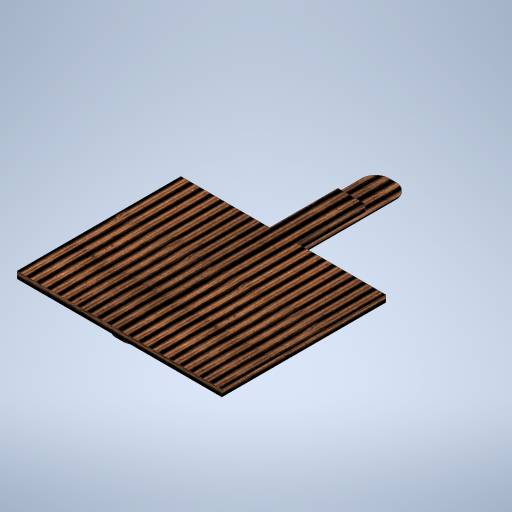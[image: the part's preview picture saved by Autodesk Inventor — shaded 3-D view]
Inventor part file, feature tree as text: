
AUTODESK INVENTOR PART (.ipt)
format: ipt  version: 2023 (Build 270158000, 158)  size: 354,304 bytes
history: native  units: in
note: dims shown in document units (in); Inventor stores cm internally (conversion verified against a paired STEP export)
features: extrude x2, sketch x2
ambient origin geometry x8: Origin, YZ Plane, XZ Plane, XY Plane, X Axis, Y Axis, Z Axis, Center Point
bodies: Solid1 (feature_tree)
feature tree (4):
  extrude  "Extrusion1"  Depth=4.7244in
  extrude  "Extrusion2"  Depth=1.9685in
  sketch  "Sketch1"  dims[d0=5.9055in d1=4.7244in]
  sketch  "Sketch2"  dims[d2=0.7874in d3=1.9685in d4=0.1969in d5=0.0in d6=0.9843in d7=7.874in d8=0.3937in d9=0.0394in d10=0.0in]
